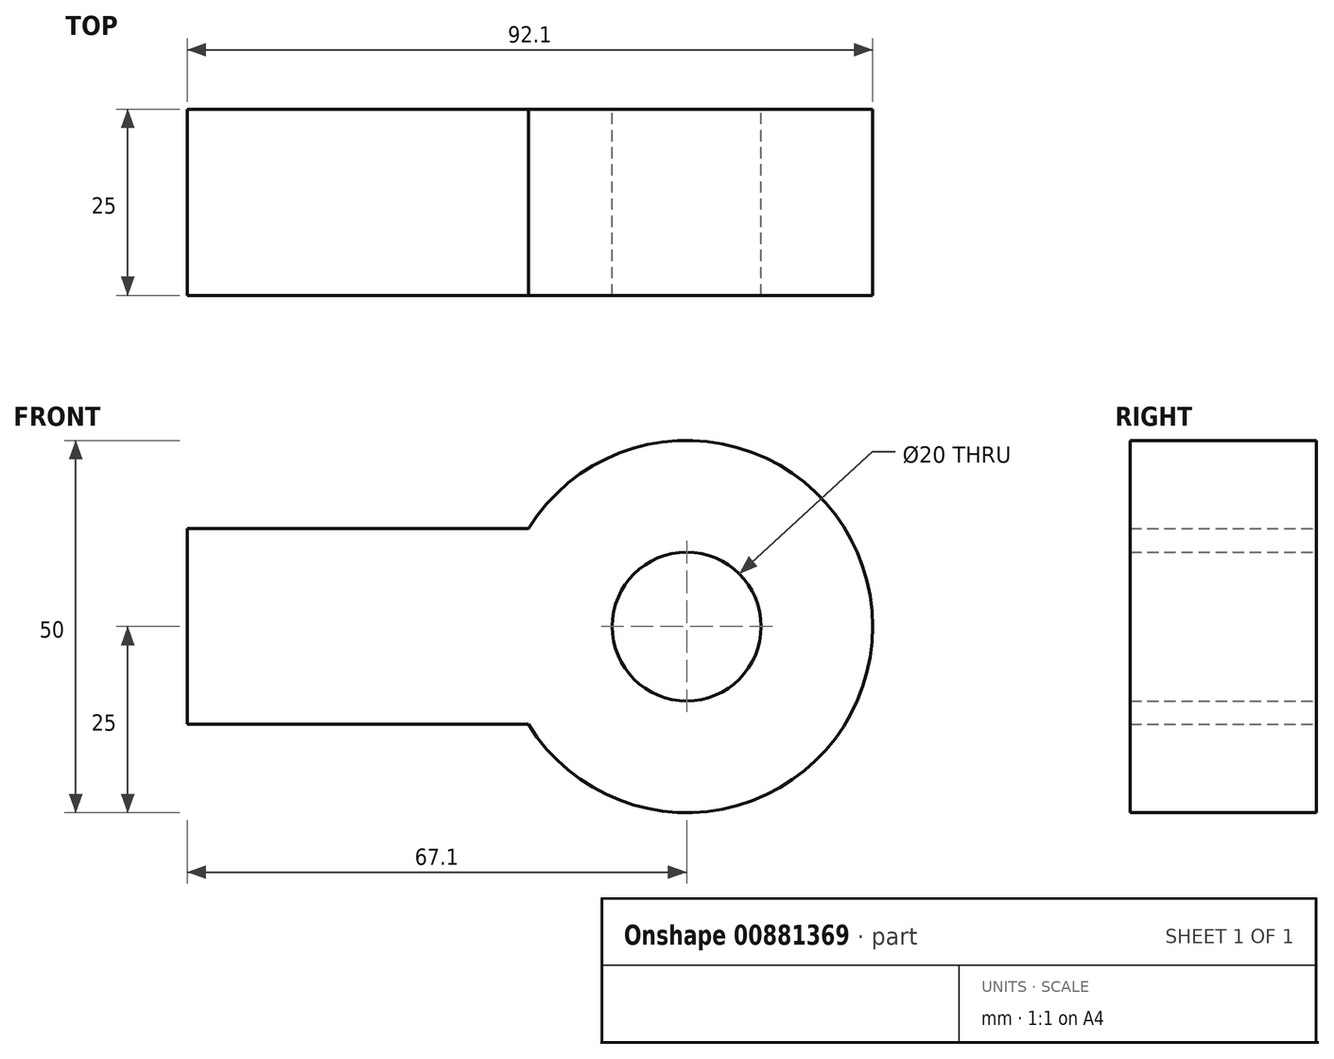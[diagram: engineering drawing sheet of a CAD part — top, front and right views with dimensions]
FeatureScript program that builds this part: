
annotation { "Feature Type Name" : "Feature", "Feature Type Description" : "" }
export const myFeature = defineFeature(function(context is Context, id is Id, definition is map)
    precondition{}
    {
        {
            var Q0;
            Q0=qCreatedBy(makeId("Front.planeOp"),FACE);
            var sketch = newSketch(context, id + "F0", { "sketchPlane" : qUnion([Q0])});
            skCircle(sketch, "E0", {"center": v(0, 0) * mm, "radius": 25 * mm});
            skCircle(sketch, "E1", {"center": v(0, 0) * mm, "radius": 10 * mm});
            skLineSegment(sketch, "E2.bottom", {"start": v(-17.16, 13.15) * mm, "end": v(-67.1, 13.15) * mm});
            skLineSegment(sketch, "E2.top", {"start": v(-17.16, -13.15) * mm, "end": v(-67.1, -13.15) * mm});
            skLineSegment(sketch, "E2.left", {"start": v(-17.16, 13.15) * mm, "end": v(-17.16, -13.15) * mm});
            skLineSegment(sketch, "E2.right", {"start": v(-67.1, 13.15) * mm, "end": v(-67.1, -13.15) * mm});
            skPoint(sketch, "E2.middle", {"position": v(-42.13, 0) * mm});
            skSolve(sketch);
        }
        {
            var Q0;
            Q0=makeQuery(id+"F0.imprint","IMPRINT",FACE,{"disambiguationData":[TD([[makeQuery(id+"F0.imprint","IMPRINT",EDGE,{"derivedFrom":sQuery(id+"F0.wireOp",EDGE,"E0")}),1.0]])]});
            var Q1;
            {var subQ5=sQuery(id+"F0.wireOp",EDGE,"E2.right");Q1=makeQuery(id+"F0.imprint","IMPRINT",FACE,{"disambiguationData":[TD([[makeQuery(id+"F0.imprint","IMPRINT",EDGE,{"derivedFrom":subQ5}),1.0]])]});}
            var Q2;
            Q2=makeQuery(id+"F0.imprint","IMPRINT",FACE,{"disambiguationData":[TD([[makeQuery(id+"F0.imprint","IMPRINT",EDGE,{"derivedFrom":sQuery(id+"F0.wireOp",EDGE,"E1")}),-1.0]])]});
            extrude(context, id + "F1", {"entities" : qUnion([Q0, Q1, Q2]), "depth" : 25 * mm, "offsetDistance" : 25 * mm});
        }
    });
